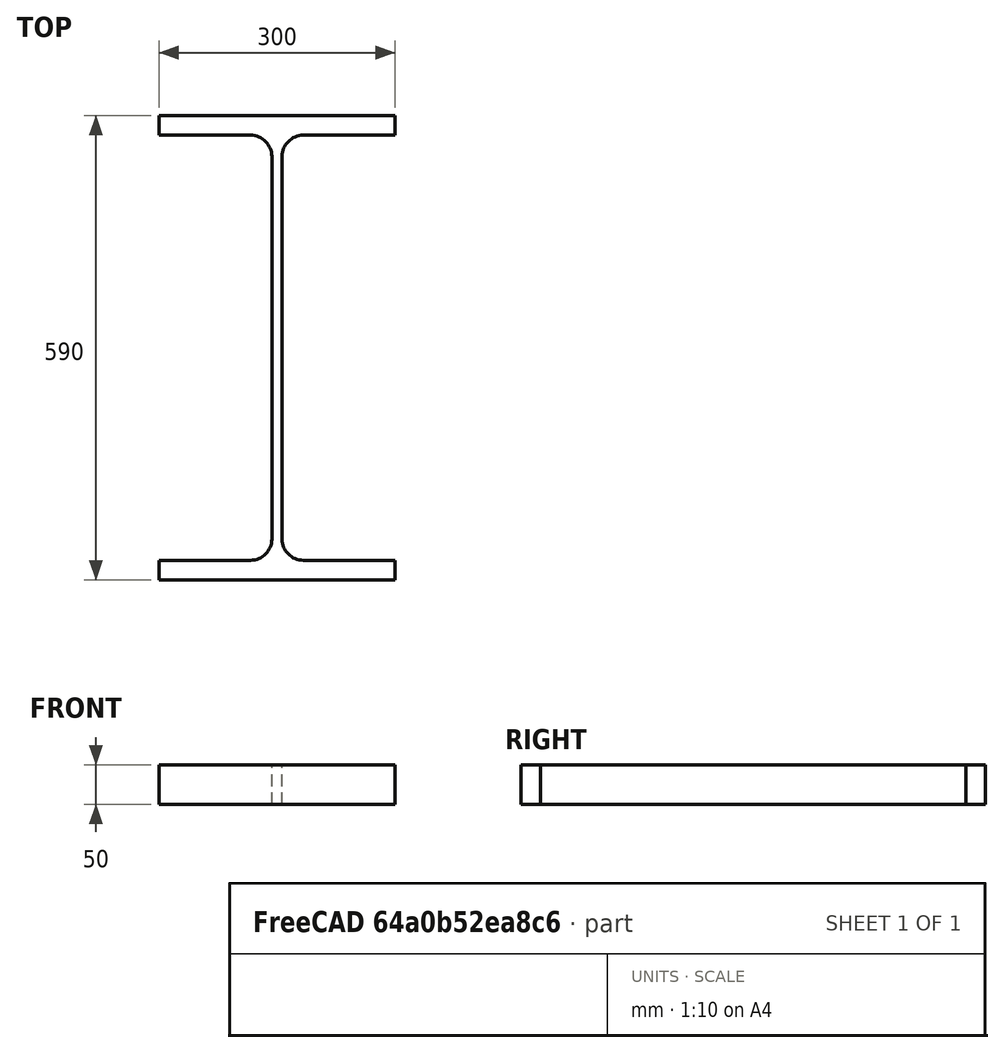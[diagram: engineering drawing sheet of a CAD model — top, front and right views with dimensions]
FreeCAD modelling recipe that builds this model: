
FCSTD DOCUMENT  (FreeCAD 0.15R4671 (Git))
Label: HE-A-Profile 600 DIN1025-3 S235JR
License: All rights reserved
LicenseURL: http://en.wikipedia.org/wiki/All_rights_reserved
objects: Sketcher::SketchObject×1, Part::Extrusion×1
note: 2 computed .brp shape members not serialized (recipe doc carries the construction recipe); baked Part::Feature solids carry a one-line shape summary decoded from their .brp

FEATURE [Sketcher::SketchObject] Sketch
  sketch-geometry (16):
    g0: LineSegment StartX=6.5 StartY=-243 StartZ=0 EndX=6.5 EndY=243 EndZ=0
    g1: LineSegment StartX=33.5 StartY=270 StartZ=0 EndX=150 EndY=270 EndZ=0
    g2: LineSegment StartX=150 StartY=270 StartZ=0 EndX=150 EndY=295 EndZ=0
    g3: LineSegment StartX=150 StartY=295 StartZ=0 EndX=-150 EndY=295 EndZ=0
    g4: LineSegment StartX=-150 StartY=295 StartZ=0 EndX=-150 EndY=270 EndZ=0
    g5: LineSegment StartX=-150 StartY=270 StartZ=0 EndX=-33.5 EndY=270 EndZ=0
    g6: LineSegment StartX=-6.5 StartY=243 StartZ=0 EndX=-6.5 EndY=-243 EndZ=0
    g7: LineSegment StartX=-33.5 StartY=-270 StartZ=0 EndX=-150 EndY=-270 EndZ=0
    g8: LineSegment StartX=-150 StartY=-270 StartZ=0 EndX=-150 EndY=-295 EndZ=0
    g9: LineSegment StartX=-150 StartY=-295 StartZ=0 EndX=150 EndY=-295 EndZ=0
    g10: LineSegment StartX=150 StartY=-295 StartZ=0 EndX=150 EndY=-270 EndZ=0
    g11: LineSegment StartX=150 StartY=-270 StartZ=0 EndX=33.5 EndY=-270 EndZ=0
    g12: ArcOfCircle CenterX=33.5 CenterY=243 CenterZ=0 NormalX=0 NormalY=0 NormalZ=1 Radius=27 StartAngle=1.5708 EndAngle=3.14159
    g13: ArcOfCircle CenterX=33.5 CenterY=-243 CenterZ=0 NormalX=0 NormalY=0 NormalZ=1 Radius=27 StartAngle=3.14159 EndAngle=4.71239
    g14: ArcOfCircle CenterX=-33.5 CenterY=243 CenterZ=0 NormalX=0 NormalY=0 NormalZ=1 Radius=27 StartAngle=0 EndAngle=1.5708
    g15: ArcOfCircle CenterX=-33.5 CenterY=-243 CenterZ=0 NormalX=0 NormalY=0 NormalZ=1 Radius=27 StartAngle=4.71239 EndAngle=6.28319
  constraints (42):
    c: Vertical(g0)
    c: Coincident(g2,g1)
    c: Vertical(g2)
    c: Coincident(g3,g2)
    c: Coincident(g4,g3)
    c: Vertical(g4)
    c: Coincident(g5,g4)
    c: Horizontal(g5)
    c: Vertical(g6)
    c: Horizontal(g7)
    c: Coincident(g8,g7)
    c: Vertical(g8)
    c: Coincident(g9,g8)
    c: Horizontal(g9)
    c: Coincident(g10,g9)
    c: Vertical(g10)
    c: Coincident(g11,g10)
    c: Horizontal(g11)
    c: Tangent(g1,g12) = 1.5708
    c: Tangent(g0,g12) = 1.5708
    c: Tangent(g0,g13) = 1.5708
    c: Tangent(g11,g13) = 1.5708
    c: Tangent(g5,g14) = 1.5708
    c: Tangent(g6,g14) = 1.5708
    c: Tangent(g6,g15) = 1.5708
    c: Tangent(g7,g15) = 1.5708
    c: Equal(g3,g9)
    c: Equal(g2,g4)
    c: Equal(g4,g8)
    c: Equal(g8,g10)
    c: Equal(g12,g14)
    c: Equal(g14,g15)
    c: Equal(g15,g13)
    c: Symmetric(g2,g3,g-2)
    c: Symmetric(g9,g8,g-2)
    c: Symmetric(g0,g6,g-2)
    c: Symmetric(g2,g9,g-1)
    c: DistanceY(g2,g9) = -590
    c: DistanceX(g3) = -300
    c: DistanceX(g0,g6) = -13
    c: DistanceY(g2) = 25
    c: Radius(g12) = 27
FEATURE [Part::Extrusion] Extrude  label="HE-A-Profile 600 DIN1025-3 S235JR"
  Base = -> Sketch
  Dir = (0,0,50)
  Solid = true
